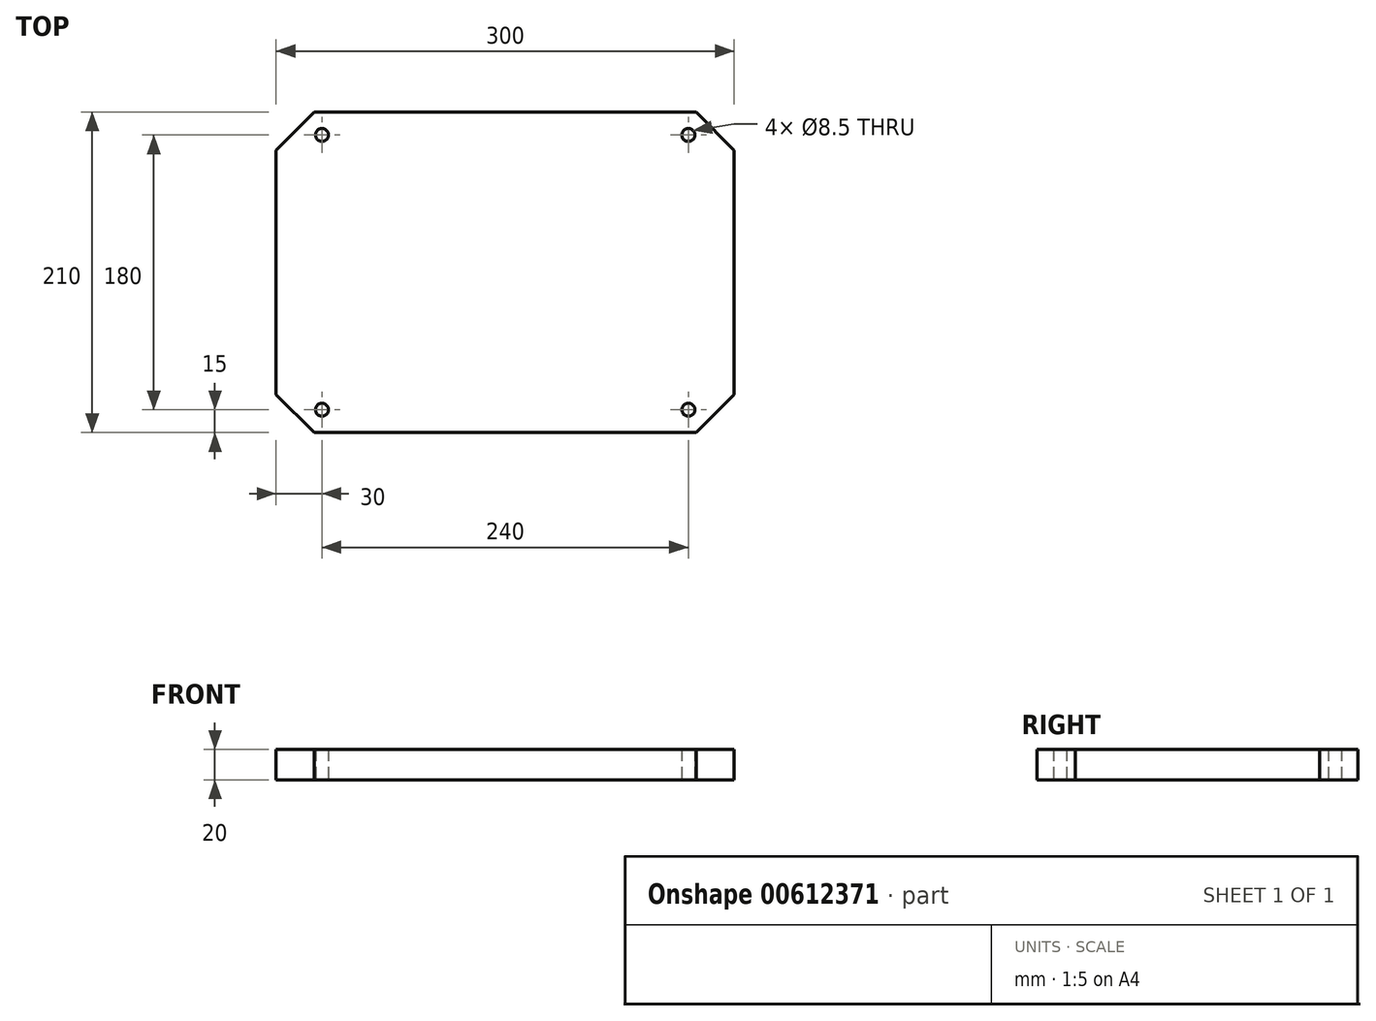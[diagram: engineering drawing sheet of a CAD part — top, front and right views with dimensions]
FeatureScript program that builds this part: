
annotation { "Feature Type Name" : "Feature", "Feature Type Description" : "" }
export const myFeature = defineFeature(function(context is Context, id is Id, definition is map)
    precondition{}
    {
        {
            var Q0;
            Q0=qCreatedBy(makeId("Top.planeOp"),FACE);
            var sketch = newSketch(context, id + "F0", { "sketchPlane" : qUnion([Q0])});
            skLineSegment(sketch, "E0.bottom", {"start": v(-150, -105) * mm, "end": v(150, -105) * mm});
            skLineSegment(sketch, "E0.top", {"start": v(-150, 105) * mm, "end": v(150, 105) * mm});
            skLineSegment(sketch, "E0.left", {"start": v(-150, -105) * mm, "end": v(-150, 105) * mm});
            skLineSegment(sketch, "E0.right", {"start": v(150, -105) * mm, "end": v(150, 105) * mm});
            skCircle(sketch, "E1", {"center": v(-120, 90) * mm, "radius": 4.25 * mm});
            skCircle(sketch, "E2", {"center": v(-120, -90) * mm, "radius": 4.25 * mm});
            skCircle(sketch, "E3", {"center": v(120, -90) * mm, "radius": 4.25 * mm});
            skCircle(sketch, "E4", {"center": v(120, 90) * mm, "radius": 4.25 * mm});
            skSolve(sketch);
        }
        {
            var Q0;
            Q0=makeQuery(id+"F0.imprint","IMPRINT",FACE,{"disambiguationData":[TD([[makeQuery(id+"F0.imprint","IMPRINT",EDGE,{"derivedFrom":sQuery(id+"F0.wireOp",EDGE,"E0.bottom")}),1.0]])]});
            extrude(context, id + "F1", {"entities" : qUnion([Q0]), "depth" : 20 * mm, "offsetDistance" : 25 * mm});
        }
        {
            var Q0;
            Q0=makeQuery(id+"F1.opExtrude","SWEPT_EDGE",EDGE,{"disambiguationData":[OSD([sQuery(id+"F0.wireOp",EDGE,"E0.bottom"),sQuery(id+"F0.wireOp",EDGE,"E0.left")])]});
            var Q1;
            Q1=makeQuery(id+"F1.opExtrude","SWEPT_EDGE",EDGE,{"disambiguationData":[OSD([sQuery(id+"F0.wireOp",EDGE,"E0.top"),sQuery(id+"F0.wireOp",EDGE,"E0.left")])]});
            var Q2;
            Q2=makeQuery(id+"F1.opExtrude","SWEPT_EDGE",EDGE,{"disambiguationData":[OSD([sQuery(id+"F0.wireOp",EDGE,"E0.bottom"),sQuery(id+"F0.wireOp",EDGE,"E0.right")])]});
            var Q3;
            Q3=makeQuery(id+"F1.opExtrude","SWEPT_EDGE",EDGE,{"disambiguationData":[OSD([sQuery(id+"F0.wireOp",EDGE,"E0.top"),sQuery(id+"F0.wireOp",EDGE,"E0.right")])]});
            chamfer(context, id + "F2", {"entities" : qUnion([Q0, Q1, Q2, Q3]), "width" : 25 * mm, "tangentPropagation" : true});
        }
    });
